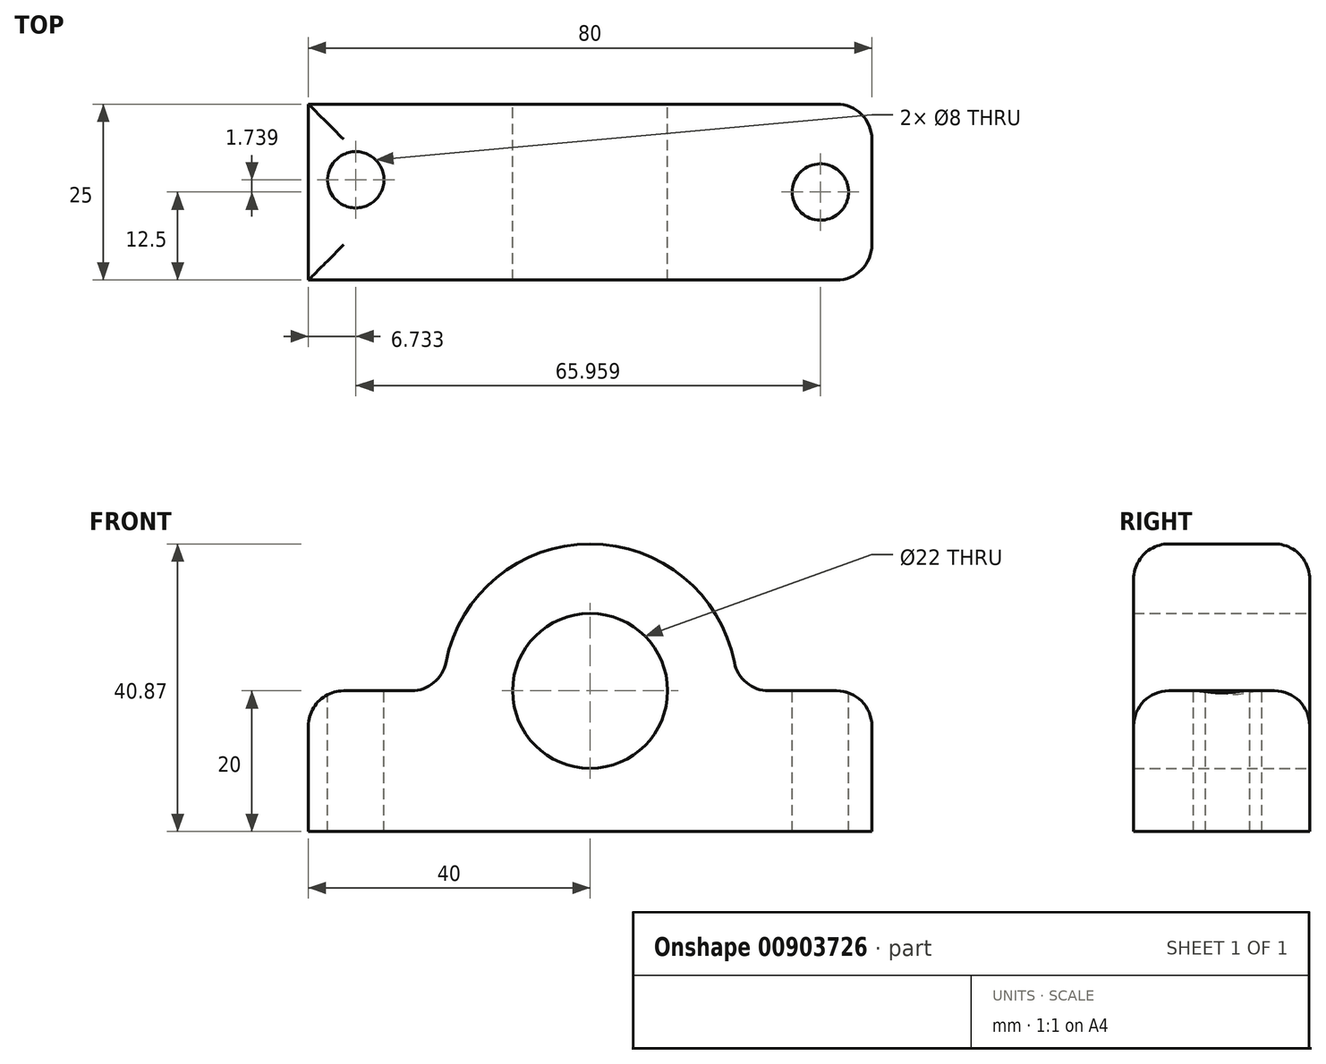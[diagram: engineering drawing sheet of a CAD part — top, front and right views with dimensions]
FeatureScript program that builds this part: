
annotation { "Feature Type Name" : "Feature", "Feature Type Description" : "" }
export const myFeature = defineFeature(function(context is Context, id is Id, definition is map)
    precondition{}
    {
        {
            var Q0;
            Q0=qCreatedBy(makeId("Front.planeOp"),FACE);
            var sketch = newSketch(context, id + "F0", { "sketchPlane" : qUnion([Q0])});
            skLineSegment(sketch, "E0.bottom", {"start": v(-40, -10) * mm, "end": v(40, -10) * mm});
            skLineSegment(sketch, "E0.top", {"start": v(-40, 10) * mm, "end": v(-25.38, 10) * mm});
            skLineSegment(sketch, "E0.left", {"start": v(-40, -10) * mm, "end": v(-40, 10) * mm});
            skLineSegment(sketch, "E0.right", {"start": v(40, -10) * mm, "end": v(40, 10) * mm});
            skPoint(sketch, "E0.middle", {"position": v(0, 0) * mm});
            skCircle(sketch, "E1", {"center": v(0, 10) * mm, "radius": 11 * mm});
            skArc(sketch, "E2", {"start": v(-20.48, 14.03) * mm, "mid": v(0, 30.87) * mm, "end": v(20.48, 14.03) * mm});
            skLineSegment(sketch, "E3.trimOffspring", {"start": v(25.38, 10) * mm, "end": v(40, 10) * mm});
            skArc(sketch, "E4.filletArc", {"start": v(20.48, 14.03) * mm, "mid": v(22.2, 11.14) * mm, "end": v(25.38, 10) * mm});
            skArc(sketch, "E5.filletArc", {"start": v(-25.38, 10) * mm, "mid": v(-22.2, 11.14) * mm, "end": v(-20.48, 14.03) * mm});
            skSolve(sketch);
        }
        {
            var Q0;
            Q0=makeQuery(id+"F0.imprint","IMPRINT",FACE,{"disambiguationData":[TD([[makeQuery(id+"F0.imprint","IMPRINT",EDGE,{"derivedFrom":sQuery(id+"F0.wireOp",EDGE,"E0.bottom")}),1.0]])]});
            extrude(context, id + "F1", {"entities" : qUnion([Q0]), "depth" : 25 * mm, "offsetDistance" : 25 * mm});
        }
        {
            var Q0;
            Q0=makeQuery(id+"F1.opExtrude","SWEPT_FACE",FACE,{"disambiguationData":[OSD([sQuery(id+"F0.wireOp",EDGE,"E3.trimOffspring")])]});
            var sketch = newSketch(context, id + "F2", { "sketchPlane" : qUnion([Q0])});
            skLineSegment(sketch, "E6", {"start": v(32.7, 0) * mm, "end": v(32.7, -25) * mm, "construction": true});
            skLineSegment(sketch, "E7", {"start": v(25.38, -12.5) * mm, "end": v(40, -12.5) * mm, "construction": true});
            skCircle(sketch, "E8", {"center": v(32.7, -12.5) * mm, "radius": 4 * mm});
            skSolve(sketch);
        }
        {
            var Q0;
            Q0=makeQuery(id+"F1.opExtrude","SWEPT_FACE",FACE,{"disambiguationData":[OSD([sQuery(id+"F0.wireOp",EDGE,"E0.top")])]});
            var sketch = newSketch(context, id + "F3", { "sketchPlane" : qUnion([Q0])});
            skCircle(sketch, "E9", {"center": v(-33.27, -10.76) * mm, "radius": 4 * mm});
            skSolve(sketch);
        }
        {
            var Q0;
            Q0=makeQuery(id+"F2.imprint","IMPRINT",FACE,{"disambiguationData":[TD([[makeQuery(id+"F2.imprint","IMPRINT",EDGE,{"derivedFrom":sQuery(id+"F2.wireOp",EDGE,"E8")}),1.0]])]});
            var Q1;
            Q1=sQuery(id+"F2.wireOp",EDGE,"E8");
            extrude(context, id + "F4", {"entities" : qUnion([Q0]), "operationType" : NewBodyOperationType.REMOVE, "surfaceEntities" : qUnion([Q1]), "oppositeDirection" : true, "depth" : 25 * mm, "offsetDistance" : 25 * mm});
        }
        {
            var Q0;
            Q0=makeQuery(id+"F3.imprint","IMPRINT",FACE,{"disambiguationData":[TD([[makeQuery(id+"F3.imprint","IMPRINT",EDGE,{"derivedFrom":sQuery(id+"F3.wireOp",EDGE,"E9")}),1.0]])]});
            extrude(context, id + "F5", {"entities" : qUnion([Q0]), "operationType" : NewBodyOperationType.REMOVE, "oppositeDirection" : true, "depth" : 25 * mm, "offsetDistance" : 25 * mm});
        }
        {
            var Q0;
            Q0=makeQuery(id+"F1.opExtrude","CAP_EDGE",EDGE,{"disambiguationData":[OSD([sQuery(id+"F0.wireOp",EDGE,"E2")])],"isStart":false});
            var Q1;
            Q1=makeQuery(id+"F1.opExtrude","SWEPT_EDGE",EDGE,{"disambiguationData":[OSD([sQuery(id+"F0.wireOp",EDGE,"E0.right"),sQuery(id+"F0.wireOp",EDGE,"E3.trimOffspring")])]});
            var Q2;
            Q2=makeQuery(id+"F1.opExtrude","CAP_EDGE",EDGE,{"disambiguationData":[OSD([sQuery(id+"F0.wireOp",EDGE,"E0.right")])],"isStart":false});
            var Q3;
            Q3=makeQuery(id+"F1.opExtrude","CAP_EDGE",EDGE,{"disambiguationData":[OSD([sQuery(id+"F0.wireOp",EDGE,"E2")])],"isStart":true});
            var Q4;
            Q4=makeQuery(id+"F1.opExtrude","SWEPT_EDGE",EDGE,{"disambiguationData":[OSD([sQuery(id+"F0.wireOp",EDGE,"E0.top"),sQuery(id+"F0.wireOp",EDGE,"E0.left")])]});
            fillet(context, id + "F6", {"entities" : qUnion([Q0, Q1, Q2, Q3, Q4]), "radius" : 5 * mm, "tangentPropagation" : true, "allowEdgeOverflow" : false});
        }
        {
            var Q0;
            Q0=makeQuery(id+"F1.opExtrude","CAP_EDGE",EDGE,{"disambiguationData":[OSD([sQuery(id+"F0.wireOp",EDGE,"E0.right")])],"isStart":true});
            fillet(context, id + "F7", {"entities" : qUnion([Q0]), "radius" : 5 * mm, "tangentPropagation" : true, "allowEdgeOverflow" : false});
        }
    });
